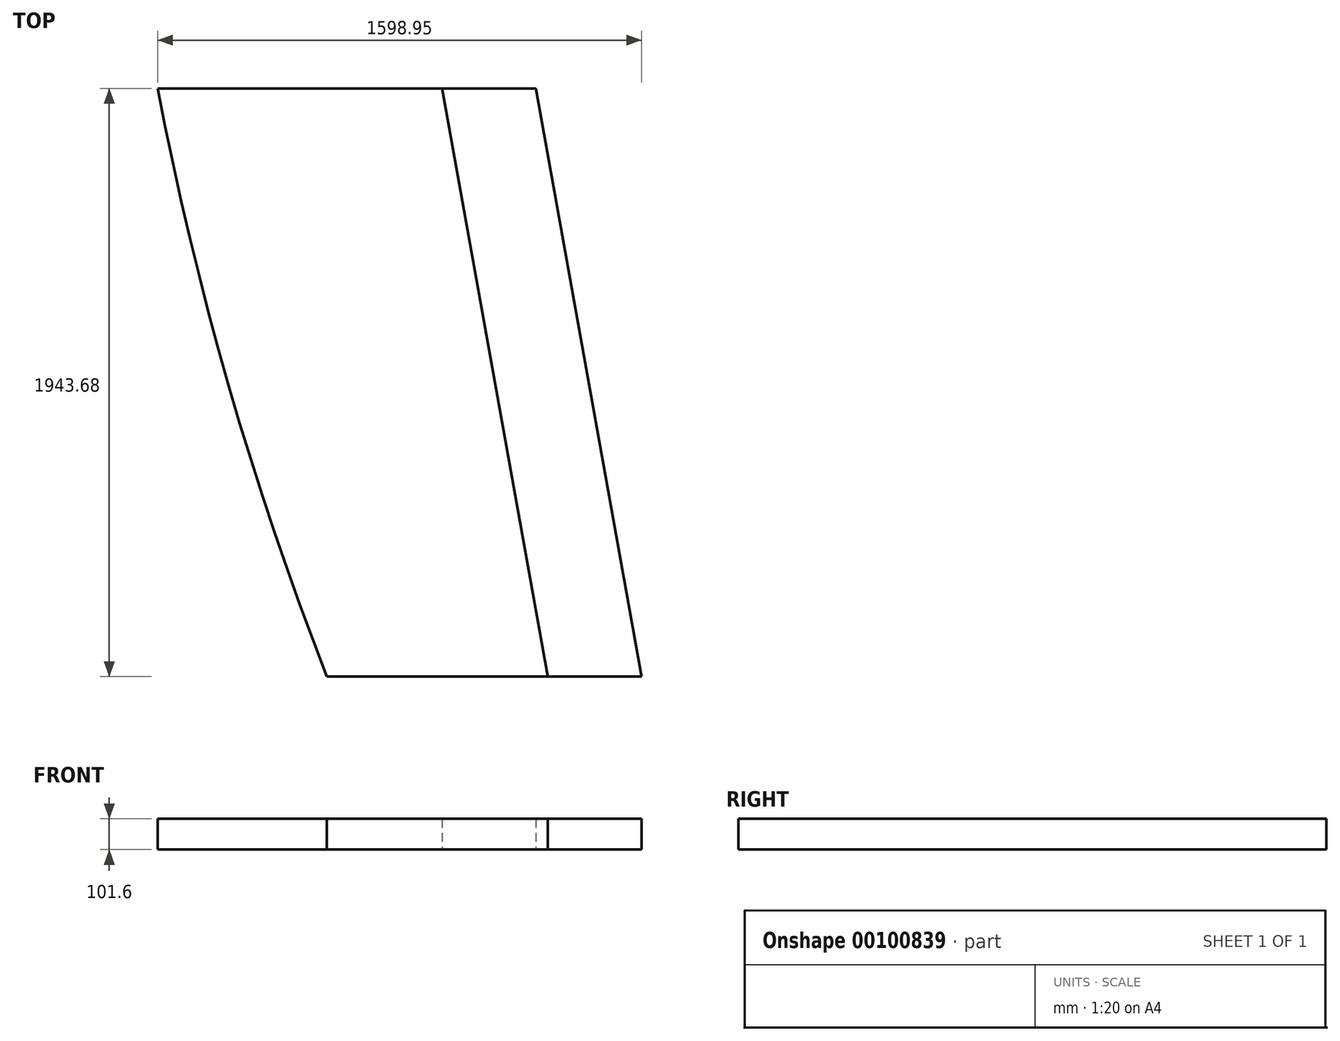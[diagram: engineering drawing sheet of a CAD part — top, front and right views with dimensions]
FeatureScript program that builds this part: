
annotation { "Feature Type Name" : "Feature", "Feature Type Description" : "" }
export const myFeature = defineFeature(function(context is Context, id is Id, definition is map)
    precondition{}
    {
        {
            var Q0;
            Q0=qCreatedBy(makeId("Top.planeOp"),FACE);
            var sketch = newSketch(context, id + "F0", { "sketchPlane" : qUnion([Q0])});
            skLineSegment(sketch, "E0", {"start": v(0, 0) * mm, "end": v(-939.8, 0) * mm});
            skLineSegment(sketch, "E1", {"start": v(-939.8, 0) * mm, "end": v(-380.78, -1943.68) * mm});
            skLineSegment(sketch, "E2", {"start": v(-380.78, -1943.68) * mm, "end": v(349.47, -1943.68) * mm});
            skLineSegment(sketch, "E3", {"start": v(349.47, -1943.68) * mm, "end": v(0, 0) * mm});
            skLineSegment(sketch, "E4", {"start": v(174.73, -971.84) * mm, "end": v(-707.92, -971.84) * mm});
            skArc(sketch, "E5", {"start": v(-939.8, 0) * mm, "mid": v(-704.29, -984.5) * mm, "end": v(-380.78, -1943.68) * mm});
            skLineSegment(sketch, "E6.0", {"start": v(659.15, -1943.68) * mm, "end": v(309.69, 0) * mm});
            skLineSegment(sketch, "E7", {"start": v(309.69, 0) * mm, "end": v(0, 0) * mm});
            skLineSegment(sketch, "E8", {"start": v(659.15, -1943.68) * mm, "end": v(349.47, -1943.68) * mm});
            skSolve(sketch);
        }
        {
            var Q0;
            {var subQ0=sQuery(id+"F0.wireOp",EDGE,"E5");var subQ3=sQuery(id+"F0.wireOp",EDGE,"E4");var subQ5=makeQuery(id+"F0.imprint","INTERSECT",VERTEX,{"derivedFrom":[subQ3,subQ0]});Q0=makeQuery(id+"F0.imprint","IMPRINT",FACE,{"disambiguationData":[TD([[makeQuery(id+"F0.imprint","IMPRINT",EDGE,{"disambiguationData":[TD([[subQ5,1.0]])],"derivedFrom":subQ3}),-1.0]])]});}
            var Q1;
            {var subQ0=sQuery(id+"F0.wireOp",EDGE,"E0");Q1=makeQuery(id+"F0.imprint","IMPRINT",FACE,{"disambiguationData":[TD([[makeQuery(id+"F0.imprint","IMPRINT",EDGE,{"derivedFrom":subQ0}),1.0]])]});}
            var Q2;
            {var subQ0=sQuery(id+"F0.wireOp",EDGE,"E5");var subQ3=sQuery(id+"F0.wireOp",EDGE,"E4");var subQ5=makeQuery(id+"F0.imprint","INTERSECT",VERTEX,{"derivedFrom":[subQ3,subQ0]});Q2=makeQuery(id+"F0.imprint","IMPRINT",FACE,{"disambiguationData":[TD([[makeQuery(id+"F0.imprint","IMPRINT",EDGE,{"disambiguationData":[TD([[subQ5,1.0]])],"derivedFrom":subQ3}),1.0]])]});}
            var Q3;
            {var subQ0=sQuery(id+"F0.wireOp",EDGE,"E2");Q3=makeQuery(id+"F0.imprint","IMPRINT",FACE,{"disambiguationData":[TD([[makeQuery(id+"F0.imprint","IMPRINT",EDGE,{"derivedFrom":subQ0}),1.0]])]});}
            extrude(context, id + "F1", {"entities" : qUnion([Q0, Q1, Q2, Q3]), "depth" : 101.6 * mm});
        }
        {
            var Q0;
            Q0=makeQuery(id+"F0.imprint","IMPRINT",FACE,{"disambiguationData":[TD([[makeQuery(id+"F0.imprint","IMPRINT",EDGE,{"derivedFrom":sQuery(id+"F0.wireOp",EDGE,"E6.0")}),1.0]])]});
            extrude(context, id + "F2", {"entities" : qUnion([Q0]), "depth" : 101.6 * mm});
        }
    });
